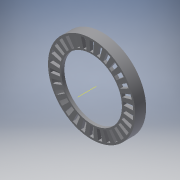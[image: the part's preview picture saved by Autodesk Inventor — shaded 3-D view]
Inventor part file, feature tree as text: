
AUTODESK INVENTOR PART (.ipt)
format: ipt  version: 2016 (Build 200138000, 138)  size: 312,832 bytes
history: native  units: mm
features: extrude x3, sketch x3, other x1, pattern_circular x1
ambient origin geometry x8: Origin, YZ Plane, XZ Plane, XY Plane, X Axis, Y Axis, Z Axis, Center Point
bodies: Body1 (feature_tree)
feature tree (8):
  extrude  "Extrusion3"  Depth=53.5mm
  extrude  "Extrusion4"  Depth=39.0mm
  other  "Work Axis3"
  pattern_circular  "Circular Pattern2"  [2 undecoded]
  extrude  "Extrusion5"  Depth=5.0mm
  sketch  "Sketch1"  dims[d0=56.0mm d1=53.5mm]
  sketch  "Sketch4"  dims[d2=41.0mm d3=39.0mm]
  sketch  "Sketch5"  dims[d13=8.5mm d17=3.0mm d18=3.0mm d19=4.0mm d20=4.0mm d21=2.0mm d22=0.0mm d23=56.0mm d24=53.5mm d25=41.0mm d26=39.0mm d27=8.5mm d28=1.0mm d29=1.0mm d30=1.304878mm d31=1.304878mm d32=10.0mm d33=0.0mm d34=300.0mm d35=360.0deg d37=5.0mm d38=0.0mm]
note: 2 required parameter values undecoded (feature->parameter linkage not recoverable at this tier; creation-order binding heuristic only, values carry confidence <= 0.55)
